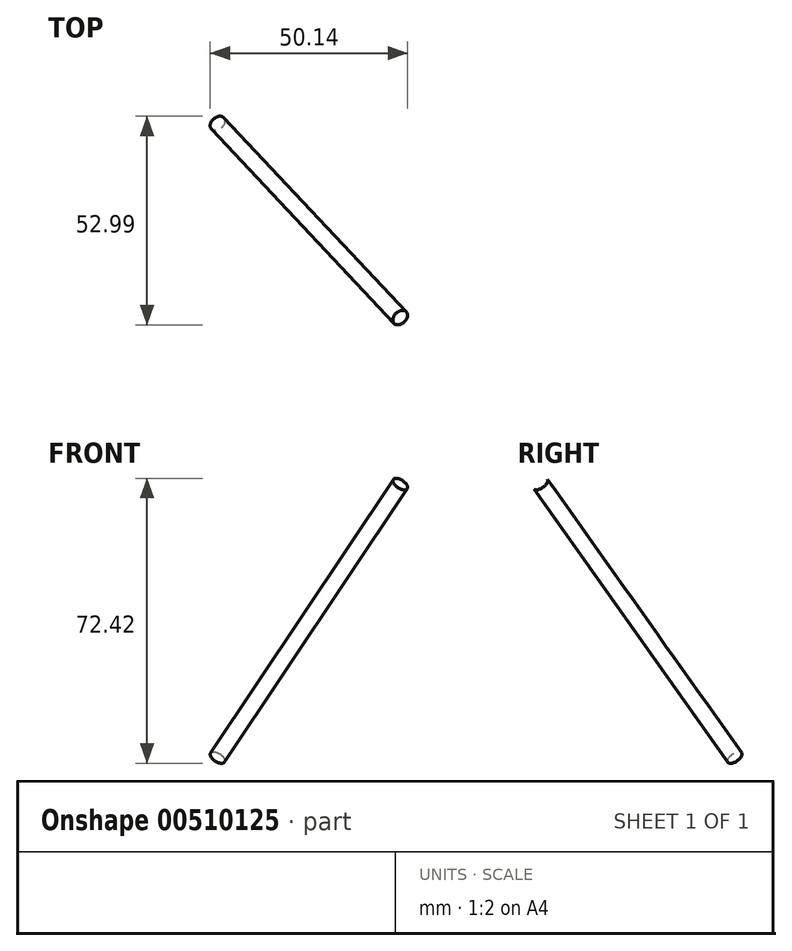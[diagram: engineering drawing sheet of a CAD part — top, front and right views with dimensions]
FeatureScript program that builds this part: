
annotation { "Feature Type Name" : "Feature", "Feature Type Description" : "" }
export const myFeature = defineFeature(function(context is Context, id is Id, definition is map)
    precondition{}
    {
        {
            var Q0;
            Q0=qCreatedBy(makeId("Front.planeOp"),FACE);
            var sketch = newSketch(context, id + "F0", { "sketchPlane" : qUnion([Q0])});
            skLineSegment(sketch, "E0", {"start": v(0, 0) * mm, "end": v(64.89, 0) * mm});
            skLineSegment(sketch, "E1", {"start": v(64.89, 0) * mm, "end": v(105.82, 0) * mm});
            skLineSegment(sketch, "E2", {"start": v(0, 0) * mm, "end": v(0, 86.72) * mm});
            skSolve(sketch);
        }
        {
            var Q0;
            Q0=qCreatedBy(makeId("Top.planeOp"),FACE);
            var sketch = newSketch(context, id + "F1", { "sketchPlane" : qUnion([Q0])});
            skLineSegment(sketch, "E3", {"start": v(0, 0) * mm, "end": v(0, -122.09) * mm});
            skSolve(sketch);
        }
        {
            var Q0;
            Q0=sQuery(id+"F0.wireOp",EDGE,"E2");
            cPoint(context, id + "F2", {"entities" : qUnion([Q0]), "parameter" : 0.5});
        }
        {
            var Q0;
            Q0=sQuery(id+"F1.wireOp",EDGE,"E3");
            cPoint(context, id + "F3", {"entities" : qUnion([Q0]), "parameter" : 0.5});
        }
        {
            var Q0;
            Q0 = qCreatedBy(id + "F2" ,VERTEX);
            var Q1;
            Q1 = qCreatedBy(id + "F3" ,VERTEX);
            var Q2;
            Q2=sQuery(id+"F0.wireOp",VERTEX,"E1.start");
            cPlane(context, id + "F4", {"entities" : qUnion([Q0, Q1, Q2]), "cplaneType" : CPlaneType.THREE_POINT, "offset" : 25.4 * mm, "width" : 152.4 * mm, "height" : 152.4 * mm});
        }
        {
            var Q0;
            Q0=qCreatedBy(id+"F4.planeOp",FACE);
            var sketch = newSketch(context, id + "F5", { "sketchPlane" : qUnion([Q0])});
            skLineSegment(sketch, "E4.bottom", {"start": v(-61.31, -56.99) * mm, "end": v(97.93, -56.99) * mm});
            skLineSegment(sketch, "E4.top", {"start": v(-61.31, 79.38) * mm, "end": v(97.93, 79.38) * mm});
            skLineSegment(sketch, "E4.left", {"start": v(-61.31, -56.99) * mm, "end": v(-61.31, 79.38) * mm});
            skLineSegment(sketch, "E4.right", {"start": v(97.93, -56.99) * mm, "end": v(97.93, 79.38) * mm});
            skSolve(sketch);
        }
        {
            var Q0;
            Q0=makeQuery(id+"F5.imprint","IMPRINT",FACE,{"disambiguationData":[TD([[makeQuery(id+"F5.imprint","IMPRINT",EDGE,{"derivedFrom":sQuery(id+"F5.wireOp",EDGE,"E4.bottom")}),1.0]])]});
            var sketch = newSketch(context, id + "F6", { "sketchPlane" : qUnion([Q0])});
            skCircle(sketch, "E5", {"center": v(16.38, 16.99) * mm, "radius": 2.12 * mm});
            skSolve(sketch);
        }
        {
            var Q0;
            Q0=makeQuery(id+"F6.imprint","IMPRINT",FACE,{"disambiguationData":[TD([[makeQuery(id+"F6.imprint","IMPRINT",EDGE,{"derivedFrom":sQuery(id+"F6.wireOp",EDGE,"E5")}),1.0]])]});
            extrude(context, id + "F7", {"entities" : qUnion([Q0]), "depth" : 97.03 * mm});
        }
    });
